# Revit family: BDG_BossDesign_Tbls_Reef_Coffee1
name_source: partatom
category: Furniture
revit_build: Autodesk Revit 2016 (Build: 20150220_1215(x64)
units: mm (PartAtom-declared; Revit-internal decimal feet)

## family parameters
Always vertical = Yes
Cut with Voids When Loaded = No
OmniClass Number = 23.40.20.00
OmniClass Title = General Furniture and Specialties
Room Calculation Point = No
Shared = Yes
Work Plane-Based = No

## types (14) — shared parameters
Assembly Code = E2020200
AssetType = Movable
BIMObjectName = BDG_BossDesign_Tables_Reef_Coffee
Category = Pr_40_50_21 : Desks, tables and worktops
DurationUnit = year
ExpectedLife = 5
IfcExportAs = IfcFurnishingElementType
IfcExportType = TABLE
Keynote = Pr_40_50_21
ManufacturerName = Boss Design
ManufacturerURL = www.bossdesign.com
NBSDescription = Tables
NBSReference = 45-35-86/327
Name = Tables_Reef_Coffee_BossDesign
NominalHeight = 425 mm  [stored 1.39436 ft]
ProductInformation = www.bossdesign.com/product-list/reef
URL = www.bossdesign.com
Uniclass2015Code = Pr_40_50_21
Uniclass2015Title = Desks, tables and worktops
Uniclass2015Version = Products v1.10
Version = 1
WarrantyDescription = Structural Warranty Excludes Foams and Fabrics
WarrantyDurationLabor = 5
WarrantyDurationParts = 5
WarrantyDurationUnit = year
zero-valued in all types: UndersideSupportOffset

## per-type parameters (varying)
| type | CircularBase | CircularTop | Description | Gap | Is2ndBase | LeftBaseOffsetforRectangleTop | LengthBetweenFeet | Model | ModelNumber | ModelReference | NominalLength | NominalLengthBaseCircle | NominalLengthBaseSquare | NominalWidth | RightBaseOffsetforRectangleTop | Shape | Size | SquareBase | SquareTop |
| 600mm x 600mm MFC top, 600mm dia base, coffee | Yes | No | 600mm x 600mm MFC top, grey, black or white 600mm dia base, coffee | 100 mm  [stored 0.328084 ft] | No | 250 mm  [stored 0.82021 ft] | 500 mm  [stored 1.64042 ft] | RF600SC C | RF600SC C | 600mm x 600mm MFC top, grey, black or white 600mm dia base, coffee | 600 mm  [stored 1.9685 ft] | 600 mm  [stored 1.9685 ft] | 600 mm  [stored 1.9685 ft] | 600 mm  [stored 1.9685 ft] | 250 mm  [stored 0.82021 ft] | Square | 600 x 600 x 425mm | No | Yes |
| 600mm dia MFC top, 600mm dia base, coffee | Yes | Yes | 600mm dia MFC top, grey, black or white 600mm dia base, coffee | 100 mm  [stored 0.328084 ft] | No | 250 mm  [stored 0.82021 ft] | 500 mm  [stored 1.64042 ft] | RF600CC C | RF600CC C | 600mm dia MFC top, grey, black or white 600mm dia base, coffee | 600 mm  [stored 1.9685 ft] | 600 mm  [stored 1.9685 ft] | 600 mm  [stored 1.9685 ft] | 600 mm  [stored 1.9685 ft] | 250 mm  [stored 0.82021 ft] | Circular | 600 ø x 425mm | No | No |
| 600mm x 600mm MFC top, 500mm x 500mm base, coffee | No | No | 600mm x 600mm MFC top, grey, black or white 500mm x 500mm base, coffee | 100 mm  [stored 0.328084 ft] | No | 200 mm  [stored 0.656168 ft] | 400 mm | RF600SS C | RF600SS C | 600mm x 600mm MFC top, grey, black or white 500mm x 500mm base, coffee | 600 mm  [stored 1.9685 ft] | 500 mm  [stored 1.64042 ft] | 500 mm  [stored 1.64042 ft] | 600 mm  [stored 1.9685 ft] | 200 mm  [stored 0.656168 ft] | Square | 600 x 600 x 425mm | Yes | Yes |
| 600mm dia MFC top, 500mm x 500mm base, coffee | No | Yes | 600mm dia MFC top, grey, black or white 500mm x 500mm base, coffee | 100 mm  [stored 0.328084 ft] | No | 200 mm  [stored 0.656168 ft] | 400 mm | RF600CS C | RF600CS C | 600mm dia MFC top, grey, black or white 500mm x 500mm base, coffee | 600 mm  [stored 1.9685 ft] | 500 mm  [stored 1.64042 ft] | 500 mm  [stored 1.64042 ft] | 600 mm  [stored 1.9685 ft] | 200 mm  [stored 0.656168 ft] | Circular | 600 ø x 425mm | Yes | No |
| 800mm x 800mm MFC top, 600mm dia base, coffee | Yes | No | 800mm x 800mm MFC top, grey, black or white 600mm dia base, coffee | 100 mm  [stored 0.328084 ft] | No | 250 mm  [stored 0.82021 ft] | 500 mm  [stored 1.64042 ft] | RF800SC C | RF800SC C | 800mm x 800mm MFC top, grey, black or white 600mm dia base, coffee | 800 mm  [stored 2.62467 ft] | 600 mm  [stored 1.9685 ft] | 600 mm  [stored 1.9685 ft] | 800 mm  [stored 2.62467 ft] | 250 mm  [stored 0.82021 ft] | Square | 800 x 800 x 425mm | No | Yes |
| 800mm dia MFC top, 600mm dia base, coffee | Yes | Yes | 800mm dia MFC top, grey, black or white 600mm dia base, coffee | 100 mm  [stored 0.328084 ft] | No | 250 mm  [stored 0.82021 ft] | 500 mm  [stored 1.64042 ft] | RF800CC C | RF800CC C | 800mm dia MFC top, grey, black or white 600mm dia base, coffee | 800 mm  [stored 2.62467 ft] | 600 mm  [stored 1.9685 ft] | 600 mm  [stored 1.9685 ft] | 800 mm  [stored 2.62467 ft] | 250 mm  [stored 0.82021 ft] | Circular | 800 ø x 425mm | No | No |
| 800mm x 800mm MFC top, 500mm x 500mm base, coffee | No | No | 800mm x 800mm MFC top, grey, black or white 500mm x 500mm base, coffee | 100 mm  [stored 0.328084 ft] | No | 200 mm  [stored 0.656168 ft] | 400 mm | RF800SS C | RF800SS C | 800mm x 800mm MFC top, grey, black or white 500mm x 500mm base, coffee | 800 mm  [stored 2.62467 ft] | 500 mm  [stored 1.64042 ft] | 500 mm  [stored 1.64042 ft] | 800 mm  [stored 2.62467 ft] | 200 mm  [stored 0.656168 ft] | Square | 800 x 800 x 425mm | Yes | Yes |
| 800mm dia MFC top, 500mm x 500mm base, coffee | No | Yes | 800mm dia MFC top, grey, black or white 500mm x 500mm base, coffee | 100 mm  [stored 0.328084 ft] | No | 200 mm  [stored 0.656168 ft] | 400 mm | RF800CS C | RF800CS C | 800mm dia MFC top, grey, black or white 500mm x 500mm base, coffee | 800 mm  [stored 2.62467 ft] | 500 mm  [stored 1.64042 ft] | 500 mm  [stored 1.64042 ft] | 800 mm  [stored 2.62467 ft] | 200 mm  [stored 0.656168 ft] | Circular | 800 ø x 425mm | Yes | No |
| 1000mm dia MFC top, 600mm dia base, coffee | Yes | Yes | 1000mm dia MFC top, grey, black or white 600mm dia base, coffee | 100 mm  [stored 0.328084 ft] | No | 250 mm  [stored 0.82021 ft] | 500 mm  [stored 1.64042 ft] | RF1000CC C | RF1000CC C | 1000mm dia MFC top, grey, black or white 600mm dia base, coffee | 1000 mm  [stored 3.28084 ft] | 600 mm  [stored 1.9685 ft] | 600 mm  [stored 1.9685 ft] | 1000 mm  [stored 3.28084 ft] | 250 mm  [stored 0.82021 ft] | Circular | 1000 ø x 425mm | No | No |
| 1000mm dia MFC top, 500mm x 500mm base, coffee | No | Yes | 1000mm dia MFC top, grey, black or white 500mm x 500mm base, coffee | 100 mm  [stored 0.328084 ft] | No | 200 mm  [stored 0.656168 ft] | 400 mm | RF1000CS C | RF1000CS C | 1000mm dia MFC top, grey, black or white 500mm x 500mm base, coffee | 1000 mm  [stored 3.28084 ft] | 500 mm  [stored 1.64042 ft] | 500 mm  [stored 1.64042 ft] | 1000 mm  [stored 3.28084 ft] | 200 mm  [stored 0.656168 ft] | Circular | 1000 ø x 425mm | Yes | No |
| 1200mm x 600mm MFC top, 500mm x 500mm base*, coffee | No | No | 1200mm x 600mm MFC top, grey, black or white 500mm x 500mm base*, coffee | 100 mm  [stored 0.328084 ft] | Yes | 500 mm  [stored 1.64042 ft] | 400 mm | RF1200CSR C | RF1200CSR C | 1200mm x 600mm MFC top, grey, black or white 500mm x 500mm base*, coffee | 1200 mm | 500 mm  [stored 1.64042 ft] | 500 mm  [stored 1.64042 ft] | 600 mm  [stored 1.9685 ft] | 500 mm  [stored 1.64042 ft] | Rectangular | 1200 x 600 x 425mm | Yes | Yes |
| 1200mm x 800mm MFC top, 500mm x 500mm base*, coffee | No | No | 1200mm x 800mm MFC top, grey, black or white 500mm x 500mm base*, coffee | 100 mm  [stored 0.328084 ft] | Yes | 500 mm  [stored 1.64042 ft] | 400 mm | RF1280CSR C | RF1280CSR C | 1200mm x 800mm MFC top, grey, black or white 500mm x 500mm base*, coffee | 1200 mm | 500 mm  [stored 1.64042 ft] | 500 mm  [stored 1.64042 ft] | 800 mm  [stored 2.62467 ft] | 500 mm  [stored 1.64042 ft] | Rectangular | 1200 x 800 x 425mm | Yes | Yes |
| 1400mm x 700mm MFC top, 500mm x 500mm base*, coffee | No | No | 1400mm x 700mm MFC top, grey, black or white 500mm x 500mm base*, coffee | 150 mm  [stored 0.492126 ft] | Yes | 500 mm  [stored 1.64042 ft] | 400 mm | RF1470CSR C | RF1470CSR C | 1400mm x 700mm MFC top, grey, black or white 500mm x 500mm base*, coffee | 1400 mm  [stored 4.59318 ft] | 500 mm  [stored 1.64042 ft] | 500 mm  [stored 1.64042 ft] | 700 mm  [stored 2.29659 ft] | 500 mm  [stored 1.64042 ft] | Rectangular | 1400 x 700 x 425mm | Yes | Yes |
| 1400mm x 700mm MFC top, 600mm dia base*, coffee | Yes | No | 1400mm x 700mm MFC top, grey, black or white 600mm dia base*, coffee | 50 mm  [stored 0.164042 ft] | Yes | 600 mm  [stored 1.9685 ft] | 500 mm  [stored 1.64042 ft] | RF1470CCR C | RF1470CCR C | 1400mm x 700mm MFC top, grey, black or white 600mm dia base*, coffee | 1400 mm  [stored 4.59318 ft] | 600 mm  [stored 1.9685 ft] | 600 mm  [stored 1.9685 ft] | 700 mm  [stored 2.29659 ft] | 600 mm  [stored 1.9685 ft] | Rectangular | 1400 x 700 x 425mm | No | Yes |

note: [stored X ft] marks values corroborated as IEEE doubles in the binary element streams (Revit-internal decimal feet)

## geometry (parser evidence)
native form markers: Sweep x1
no freeform markers — native parametric forms only
